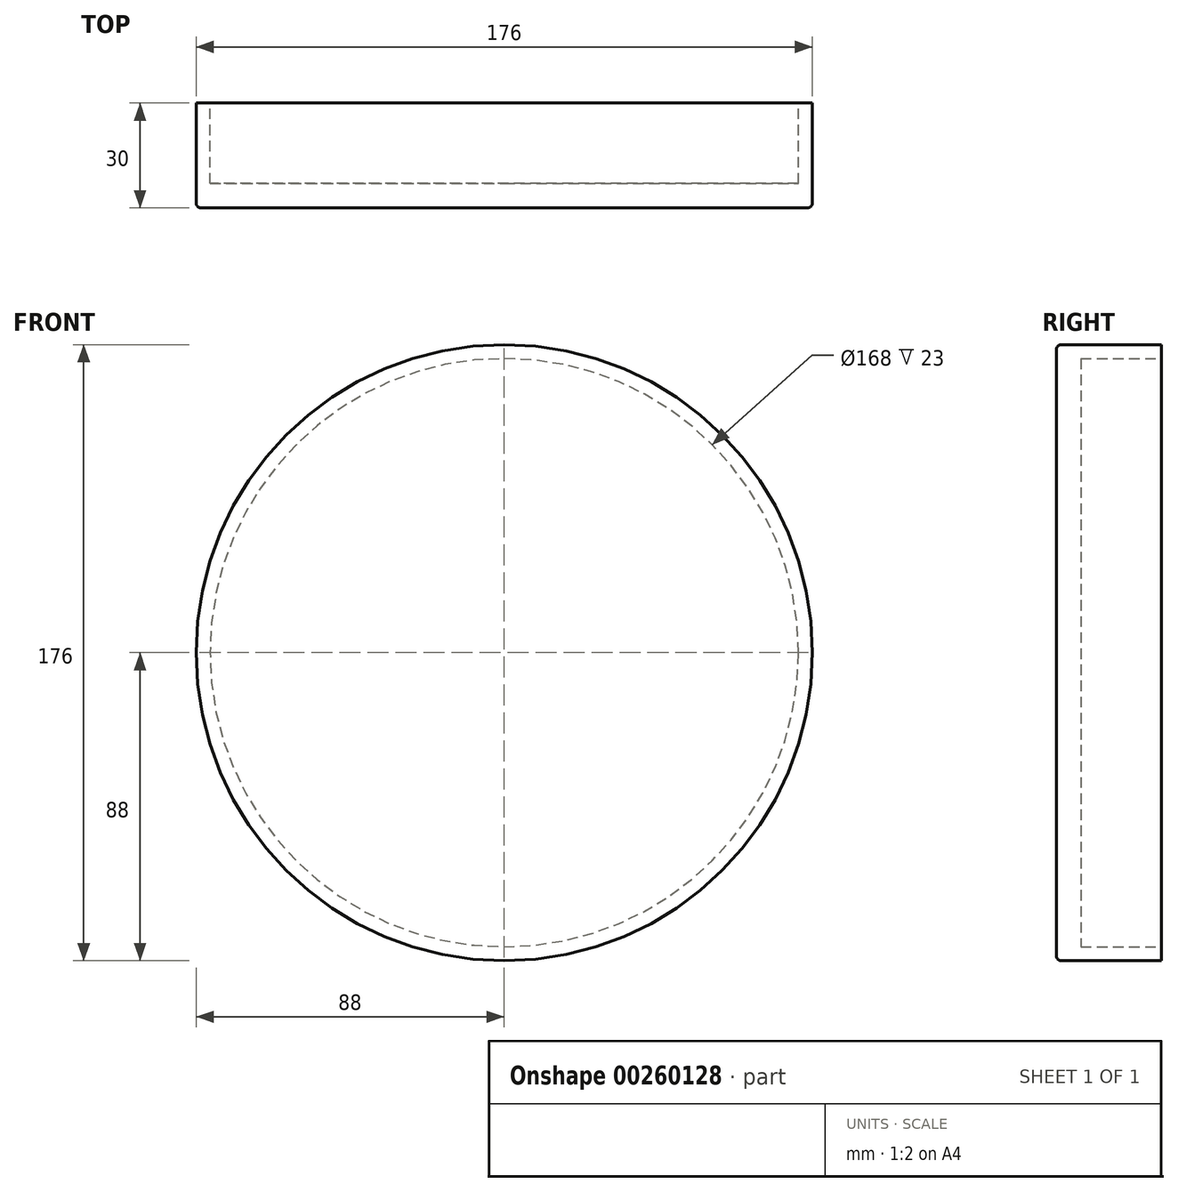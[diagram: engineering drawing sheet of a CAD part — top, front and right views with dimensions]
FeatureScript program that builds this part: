
annotation { "Feature Type Name" : "Feature", "Feature Type Description" : "" }
export const myFeature = defineFeature(function(context is Context, id is Id, definition is map)
    precondition{}
    {
        {
            var Q0;
            Q0=qCreatedBy(makeId("Front.planeOp"),FACE);
            var sketch = newSketch(context, id + "F0", { "sketchPlane" : qUnion([Q0])});
            skCircle(sketch, "E0", {"center": v(0, 0) * mm, "radius": 88 * mm});
            skSolve(sketch);
        }
        {
            var Q0;
            Q0=makeQuery(id+"F0.imprint","IMPRINT",FACE,{"disambiguationData":[TD([[makeQuery(id+"F0.imprint","IMPRINT",EDGE,{"derivedFrom":sQuery(id+"F0.wireOp",EDGE,"E0")}),1.0]])]});
            var Q1;
            Q1=sQuery(id+"F0.wireOp",EDGE,"E0");
            extrude(context, id + "F1", {"entities" : qUnion([Q0]), "surfaceEntities" : qUnion([Q1]), "depth" : 30 * mm});
        }
        {
            var Q0;
            Q0=makeQuery(id+"F1.opExtrude","CAP_FACE",FACE,{"disambiguationData":[OSD([sQuery(id+"F0.wireOp",EDGE,"E0")])],"isStart":true});
            var sketch = newSketch(context, id + "F2", { "sketchPlane" : qUnion([Q0])});
            skCircle(sketch, "E1", {"center": v(0, 0) * mm, "radius": 84 * mm});
            skSolve(sketch);
        }
        {
            var Q0;
            Q0=qSketchRegion(id+"F2",true);
            var Q1;
            Q1=qSketchRegion(id+"F9u2Kz7b36xQZs2_1",true);
            extrude(context, id + "F3", {"entities" : qUnion([Q0, Q1]), "operationType" : NewBodyOperationType.REMOVE, "oppositeDirection" : true, "depth" : 23 * mm});
        }
        {
            var Q0;
            Q0=makeQuery(id+"F1.opExtrude","CAP_EDGE",EDGE,{"disambiguationData":[OSD([sQuery(id+"F0.wireOp",EDGE,"E0")])],"isStart":false});
            fillet(context, id + "F4", {"entities" : qUnion([Q0]), "radius" : 1.5 * mm, "tangentPropagation" : true, "allowEdgeOverflow" : false});
        }
    });
